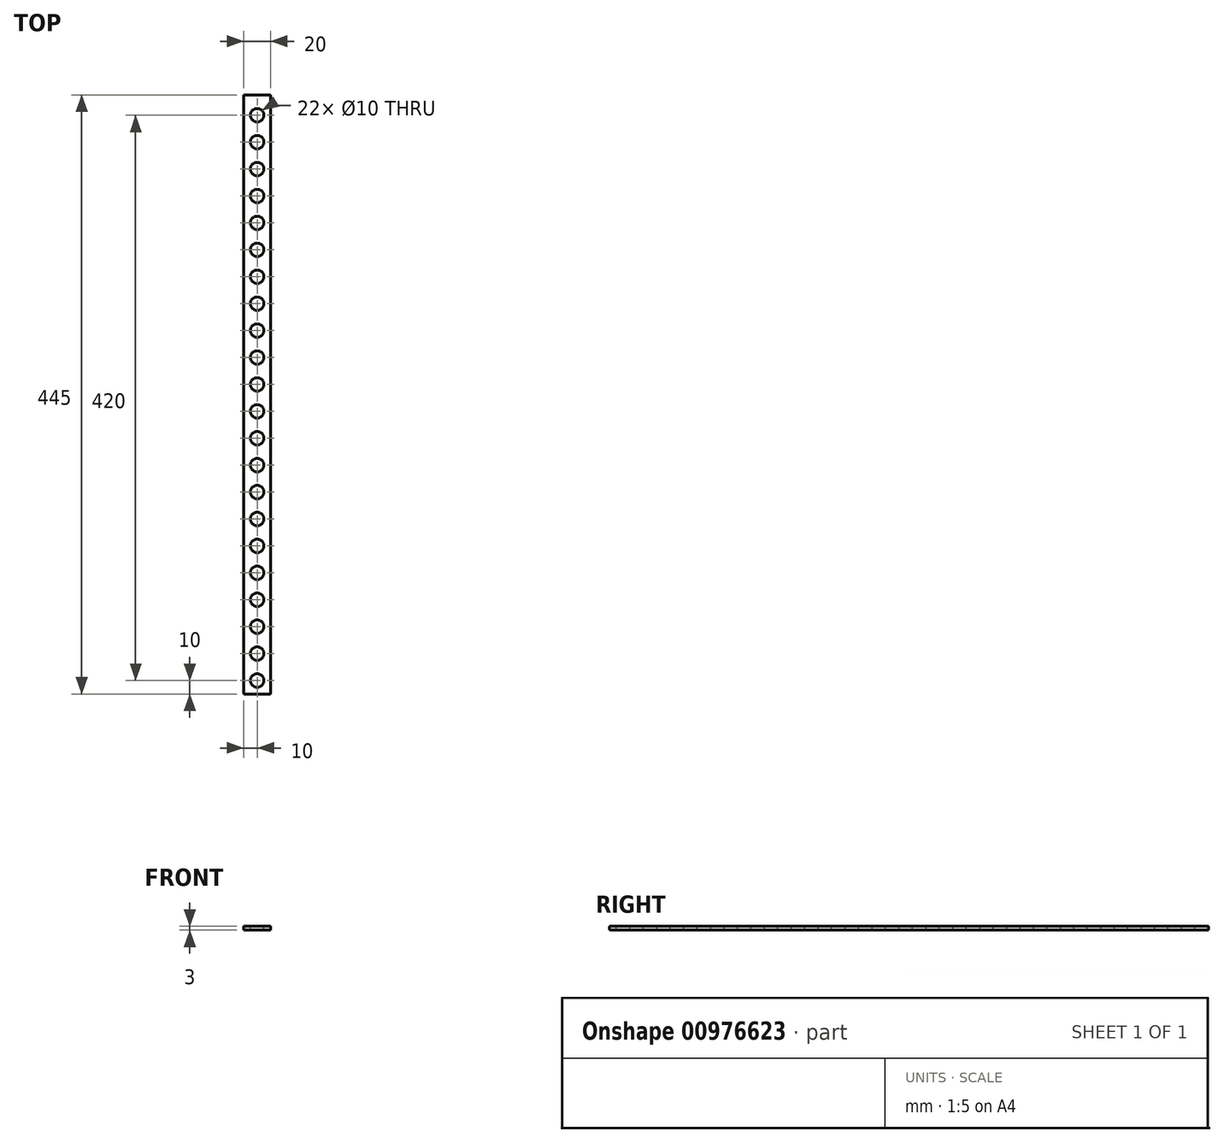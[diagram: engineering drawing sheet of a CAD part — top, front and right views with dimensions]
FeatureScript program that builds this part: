
annotation { "Feature Type Name" : "Feature", "Feature Type Description" : "" }
export const myFeature = defineFeature(function(context is Context, id is Id, definition is map)
    precondition{}
    {
        {
            var Q0;
            Q0=qCreatedBy(makeId("Front.planeOp"),FACE);
            var sketch = newSketch(context, id + "F0", { "sketchPlane" : qUnion([Q0])});
            skLineSegment(sketch, "E0.bottom", {"start": v(10, 1.5) * mm, "end": v(-10, 1.5) * mm});
            skLineSegment(sketch, "E0.top", {"start": v(10, -1.5) * mm, "end": v(-10, -1.5) * mm});
            skLineSegment(sketch, "E0.left", {"start": v(10, 1.5) * mm, "end": v(10, -1.5) * mm});
            skLineSegment(sketch, "E0.right", {"start": v(-10, 1.5) * mm, "end": v(-10, -1.5) * mm});
            skPoint(sketch, "E0.middle", {"position": v(0, 0) * mm});
            skSolve(sketch);
        }
        {
            var Q0;
            Q0=qSketchRegion(id+"F0",true);
            extrude(context, id + "F1", {"entities" : qUnion([Q0]), "depth" : 500 * mm, "offsetDistance" : 25 * mm, "symmetric" : true});
        }
        {
            var Q0;
            Q0=makeQuery(id+"F1.opExtrude","SWEPT_FACE",FACE,{"disambiguationData":[OSD([sQuery(id+"F0.wireOp",EDGE,"E0.bottom")])]});
            var sketch = newSketch(context, id + "F2", { "sketchPlane" : qUnion([Q0])});
            skLineSegment(sketch, "E1", {"start": v(0, -250) * mm, "end": v(0, -240) * mm});
            skCircle(sketch, "E2", {"center": v(0, -235) * mm, "radius": 5 * mm});
            skLineSegment(sketch, "E3", {"start": v(0, -235) * mm, "end": v(0, -215) * mm});
            skCircle(sketch, "E4.1.0.0", {"center": v(0, -215) * mm, "radius": 5 * mm});
            skCircle(sketch, "E4.2.0.0", {"center": v(0, -195) * mm, "radius": 5 * mm});
            skCircle(sketch, "E4.3.0.0", {"center": v(0, -175) * mm, "radius": 5 * mm});
            skCircle(sketch, "E4.4.0.0", {"center": v(0, -155) * mm, "radius": 5 * mm});
            skCircle(sketch, "E4.5.0.0", {"center": v(0, -135) * mm, "radius": 5 * mm});
            skCircle(sketch, "E4.6.0.0", {"center": v(0, -115) * mm, "radius": 5 * mm});
            skCircle(sketch, "E4.7.0.0", {"center": v(0, -95) * mm, "radius": 5 * mm});
            skCircle(sketch, "E4.8.0.0", {"center": v(0, -75) * mm, "radius": 5 * mm});
            skCircle(sketch, "E4.9.0.0", {"center": v(0, -55) * mm, "radius": 5 * mm});
            skCircle(sketch, "E4.10.0.0", {"center": v(0, -35) * mm, "radius": 5 * mm});
            skCircle(sketch, "E4.11.0.0", {"center": v(0, -15) * mm, "radius": 5 * mm});
            skCircle(sketch, "E4.12.0.0", {"center": v(0, 5) * mm, "radius": 5 * mm});
            skCircle(sketch, "E4.13.0.0", {"center": v(0, 25) * mm, "radius": 5 * mm});
            skCircle(sketch, "E4.14.0.0", {"center": v(0, 45) * mm, "radius": 5 * mm});
            skCircle(sketch, "E4.15.0.0", {"center": v(0, 65) * mm, "radius": 5 * mm});
            skCircle(sketch, "E4.16.0.0", {"center": v(0, 85) * mm, "radius": 5 * mm});
            skCircle(sketch, "E4.17.0.0", {"center": v(0, 105) * mm, "radius": 5 * mm});
            skCircle(sketch, "E4.18.0.0", {"center": v(0, 125) * mm, "radius": 5 * mm});
            skCircle(sketch, "E4.19.0.0", {"center": v(0, 145) * mm, "radius": 5 * mm});
            skCircle(sketch, "E4.20.0.0", {"center": v(0, 165) * mm, "radius": 5 * mm});
            skCircle(sketch, "E4.21.0.0", {"center": v(0, 185) * mm, "radius": 5 * mm});
            skCircle(sketch, "E4.22.0.0", {"center": v(0, 205) * mm, "radius": 5 * mm});
            skCircle(sketch, "E4.23.0.0", {"center": v(0, 225) * mm, "radius": 5 * mm});
            skCircle(sketch, "E4.24.0.0", {"center": v(0, 245) * mm, "radius": 5 * mm});
            skLineSegment(sketch, "E4.direction1", {"start": v(0, -235) * mm, "end": v(0, -215) * mm, "construction": true});
            skSolve(sketch);
        }
        {
            var Q0;
            Q0=makeQuery(id+"F1.opExtrude","CAP_FACE",FACE,{"disambiguationData":[OSD([sQuery(id+"F0.wireOp",EDGE,"E0.bottom"),sQuery(id+"F0.wireOp",EDGE,"E0.top"),sQuery(id+"F0.wireOp",EDGE,"E0.left"),sQuery(id+"F0.wireOp",EDGE,"E0.right")])],"isStart":true});
            extrude(context, id + "F3", {"entities" : qUnion([Q0]), "operationType" : NewBodyOperationType.ADD, "depth" : 10 * mm, "offsetDistance" : 25 * mm});
        }
        {
            var Q0;
            {var subQ0=sQuery(id+"F2.wireOp",EDGE,"E2");var subQ1=makeQuery(id+"F2.imprint","IMPRINT",VERTEX,{"disambiguationData":[OD(0.0)],"derivedFrom":subQ0});Q0=makeQuery(id+"F2.imprint","IMPRINT",FACE,{"disambiguationData":[TD([[makeQuery(id+"F2.imprint","IMPRINT",EDGE,{"disambiguationData":[TD([[subQ1,1.0]])],"derivedFrom":subQ0}),1.0]])]});}
            var Q1;
            Q1=makeQuery(id+"F2.imprint","IMPRINT",FACE,{"disambiguationData":[TD([[makeQuery(id+"F2.imprint","IMPRINT",EDGE,{"derivedFrom":sQuery(id+"F2.wireOp",EDGE,"E4.1.0.0")}),1.0]])]});
            var Q2;
            Q2=makeQuery(id+"F2.imprint","IMPRINT",FACE,{"disambiguationData":[TD([[makeQuery(id+"F2.imprint","IMPRINT",EDGE,{"derivedFrom":sQuery(id+"F2.wireOp",EDGE,"E4.2.0.0")}),1.0]])]});
            var Q3;
            Q3=makeQuery(id+"F2.imprint","IMPRINT",FACE,{"disambiguationData":[TD([[makeQuery(id+"F2.imprint","IMPRINT",EDGE,{"derivedFrom":sQuery(id+"F2.wireOp",EDGE,"E4.3.0.0")}),1.0]])]});
            var Q4;
            Q4=makeQuery(id+"F2.imprint","IMPRINT",FACE,{"disambiguationData":[TD([[makeQuery(id+"F2.imprint","IMPRINT",EDGE,{"derivedFrom":sQuery(id+"F2.wireOp",EDGE,"E4.4.0.0")}),1.0]])]});
            var Q5;
            Q5=makeQuery(id+"F2.imprint","IMPRINT",FACE,{"disambiguationData":[TD([[makeQuery(id+"F2.imprint","IMPRINT",EDGE,{"derivedFrom":sQuery(id+"F2.wireOp",EDGE,"E4.5.0.0")}),1.0]])]});
            var Q6;
            Q6=makeQuery(id+"F2.imprint","IMPRINT",FACE,{"disambiguationData":[TD([[makeQuery(id+"F2.imprint","IMPRINT",EDGE,{"derivedFrom":sQuery(id+"F2.wireOp",EDGE,"E4.6.0.0")}),1.0]])]});
            var Q7;
            Q7=makeQuery(id+"F2.imprint","IMPRINT",FACE,{"disambiguationData":[TD([[makeQuery(id+"F2.imprint","IMPRINT",EDGE,{"derivedFrom":sQuery(id+"F2.wireOp",EDGE,"E4.7.0.0")}),1.0]])]});
            var Q8;
            Q8=makeQuery(id+"F2.imprint","IMPRINT",FACE,{"disambiguationData":[TD([[makeQuery(id+"F2.imprint","IMPRINT",EDGE,{"derivedFrom":sQuery(id+"F2.wireOp",EDGE,"E4.8.0.0")}),1.0]])]});
            var Q9;
            Q9=makeQuery(id+"F2.imprint","IMPRINT",FACE,{"disambiguationData":[TD([[makeQuery(id+"F2.imprint","IMPRINT",EDGE,{"derivedFrom":sQuery(id+"F2.wireOp",EDGE,"E4.9.0.0")}),1.0]])]});
            var Q10;
            Q10=makeQuery(id+"F2.imprint","IMPRINT",FACE,{"disambiguationData":[TD([[makeQuery(id+"F2.imprint","IMPRINT",EDGE,{"derivedFrom":sQuery(id+"F2.wireOp",EDGE,"E4.10.0.0")}),1.0]])]});
            var Q11;
            Q11=makeQuery(id+"F2.imprint","IMPRINT",FACE,{"disambiguationData":[TD([[makeQuery(id+"F2.imprint","IMPRINT",EDGE,{"derivedFrom":sQuery(id+"F2.wireOp",EDGE,"E4.11.0.0")}),1.0]])]});
            var Q12;
            Q12=makeQuery(id+"F2.imprint","IMPRINT",FACE,{"disambiguationData":[TD([[makeQuery(id+"F2.imprint","IMPRINT",EDGE,{"derivedFrom":sQuery(id+"F2.wireOp",EDGE,"E4.12.0.0")}),1.0]])]});
            var Q13;
            Q13=makeQuery(id+"F2.imprint","IMPRINT",FACE,{"disambiguationData":[TD([[makeQuery(id+"F2.imprint","IMPRINT",EDGE,{"derivedFrom":sQuery(id+"F2.wireOp",EDGE,"E4.15.0.0")}),1.0]])]});
            var Q14;
            Q14=makeQuery(id+"F2.imprint","IMPRINT",FACE,{"disambiguationData":[TD([[makeQuery(id+"F2.imprint","IMPRINT",EDGE,{"derivedFrom":sQuery(id+"F2.wireOp",EDGE,"E4.16.0.0")}),1.0]])]});
            var Q15;
            Q15=makeQuery(id+"F2.imprint","IMPRINT",FACE,{"disambiguationData":[TD([[makeQuery(id+"F2.imprint","IMPRINT",EDGE,{"derivedFrom":sQuery(id+"F2.wireOp",EDGE,"E4.17.0.0")}),1.0]])]});
            var Q16;
            Q16=makeQuery(id+"F2.imprint","IMPRINT",FACE,{"disambiguationData":[TD([[makeQuery(id+"F2.imprint","IMPRINT",EDGE,{"derivedFrom":sQuery(id+"F2.wireOp",EDGE,"E4.18.0.0")}),1.0]])]});
            var Q17;
            Q17=makeQuery(id+"F2.imprint","IMPRINT",FACE,{"disambiguationData":[TD([[makeQuery(id+"F2.imprint","IMPRINT",EDGE,{"derivedFrom":sQuery(id+"F2.wireOp",EDGE,"E4.14.0.0")}),1.0]])]});
            var Q18;
            Q18=makeQuery(id+"F2.imprint","IMPRINT",FACE,{"disambiguationData":[TD([[makeQuery(id+"F2.imprint","IMPRINT",EDGE,{"derivedFrom":sQuery(id+"F2.wireOp",EDGE,"E4.13.0.0")}),1.0]])]});
            var Q19;
            Q19=makeQuery(id+"F2.imprint","IMPRINT",FACE,{"disambiguationData":[TD([[makeQuery(id+"F2.imprint","IMPRINT",EDGE,{"derivedFrom":sQuery(id+"F2.wireOp",EDGE,"E4.19.0.0")}),1.0]])]});
            var Q20;
            Q20=makeQuery(id+"F2.imprint","IMPRINT",FACE,{"disambiguationData":[TD([[makeQuery(id+"F2.imprint","IMPRINT",EDGE,{"derivedFrom":sQuery(id+"F2.wireOp",EDGE,"E4.20.0.0")}),1.0]])]});
            var Q21;
            Q21=makeQuery(id+"F2.imprint","IMPRINT",FACE,{"disambiguationData":[TD([[makeQuery(id+"F2.imprint","IMPRINT",EDGE,{"derivedFrom":sQuery(id+"F2.wireOp",EDGE,"E4.21.0.0")}),1.0]])]});
            var Q22;
            Q22=makeQuery(id+"F2.imprint","IMPRINT",FACE,{"disambiguationData":[TD([[makeQuery(id+"F2.imprint","IMPRINT",EDGE,{"derivedFrom":sQuery(id+"F2.wireOp",EDGE,"E4.22.0.0")}),1.0]])]});
            var Q23;
            Q23=makeQuery(id+"F2.imprint","IMPRINT",FACE,{"disambiguationData":[TD([[makeQuery(id+"F2.imprint","IMPRINT",EDGE,{"derivedFrom":sQuery(id+"F2.wireOp",EDGE,"E4.23.0.0")}),1.0]])]});
            var Q24;
            Q24=makeQuery(id+"F2.imprint","IMPRINT",FACE,{"disambiguationData":[TD([[makeQuery(id+"F2.imprint","IMPRINT",EDGE,{"derivedFrom":sQuery(id+"F2.wireOp",EDGE,"E4.24.0.0")}),1.0]])]});
            extrude(context, id + "F4", {"entities" : qUnion([Q0, Q1, Q2, Q3, Q4, Q5, Q6, Q7, Q8, Q9, Q10, Q11, Q12, Q13, Q14, Q15, Q16, Q17, Q18, Q19, Q20, Q21, Q22, Q23, Q24]), "operationType" : NewBodyOperationType.REMOVE, "oppositeDirection" : true, "depth" : 3 * mm, "offsetDistance" : 25 * mm});
        }
        {
            var Q0;
            {var subQ0=sQuery(id+"F0.wireOp",EDGE,"E0.left");Q0=makeQuery(id+"F3.boolean.opBoolean","MERGE",FACE,{"derivedFrom":[makeQuery(id+"F1.opExtrude","SWEPT_FACE",FACE,{"disambiguationData":[OSD([subQ0])]}),makeQuery(id+"F3.opExtrude","SWEPT_FACE",FACE,{"disambiguationData":[OSD([subQ0])]})]});}
            var Q1;
            Q1=makeQuery(id+"F1.opExtrude","CAP_FACE",FACE,{"disambiguationData":[OSD([sQuery(id+"F0.wireOp",EDGE,"E0.bottom"),sQuery(id+"F0.wireOp",EDGE,"E0.top"),sQuery(id+"F0.wireOp",EDGE,"E0.left"),sQuery(id+"F0.wireOp",EDGE,"E0.right")])],"isStart":false});
            var Q2;
            {var subQ0=sQuery(id+"F0.wireOp",EDGE,"E0.right");var subQ1=sQuery(id+"F0.wireOp",EDGE,"E0.bottom");Q2=makeQuery(id+"F3.boolean.opBoolean","MERGE",EDGE,{"derivedFrom":[makeQuery(id+"F1.opExtrude","SWEPT_EDGE",EDGE,{"disambiguationData":[OSD([subQ1,subQ0])]}),makeQuery(id+"F3.opExtrude","SWEPT_EDGE",EDGE,{"disambiguationData":[OSD([subQ1,subQ0])]})]});}
            var Q3;
            Q3=makeQuery(id+"F3.opExtrude","CAP_FACE",FACE,{"disambiguationData":[OSD([sQuery(id+"F0.wireOp",EDGE,"E0.bottom"),sQuery(id+"F0.wireOp",EDGE,"E0.top"),sQuery(id+"F0.wireOp",EDGE,"E0.left"),sQuery(id+"F0.wireOp",EDGE,"E0.right")])],"isStart":false});
            fillet(context, id + "F5", {"entities" : qUnion([Q0, Q1, Q2, Q3]), "radius" : .5 * mm, "tangentPropagation" : true, "allowEdgeOverflow" : false});
        }
        {
            var Q0;
            {var subQ0=sQuery(id+"F0.wireOp",EDGE,"E0.top");Q0=makeQuery(id+"F3.boolean.opBoolean","MERGE",FACE,{"derivedFrom":[makeQuery(id+"F1.opExtrude","SWEPT_FACE",FACE,{"disambiguationData":[OSD([subQ0])]}),makeQuery(id+"F3.opExtrude","SWEPT_FACE",FACE,{"disambiguationData":[OSD([subQ0])]})]});}
            var sketch = newSketch(context, id + "F6", { "sketchPlane" : qUnion([Q0])});
            skLineSegment(sketch, "E5", {"start": v(0, 195) * mm, "end": v(0, 185) * mm});
            skLineSegment(sketch, "E6", {"start": v(16.08, 185) * mm, "end": v(-14.65, 185) * mm});
            skLineSegment(sketch, "E7", {"start": v(-14.65, 254.38) * mm, "end": v(32.46, 259.38) * mm});
            skLineSegment(sketch, "E8", {"start": v(32.46, 259.38) * mm, "end": v(16.08, 185) * mm});
            skLineSegment(sketch, "E9", {"start": v(-14.65, 254.38) * mm, "end": v(-14.65, 185) * mm});
            skSolve(sketch);
        }
        {
            var Q0;
            Q0=qSketchRegion(id+"F6",true);
            extrude(context, id + "F7", {"entities" : qUnion([Q0]), "operationType" : NewBodyOperationType.REMOVE, "oppositeDirection" : true, "depth" : 25 * mm, "offsetDistance" : 25 * mm});
        }
        {
            var Q0;
            Q0=makeQuery(id+"F7.boolean.opBoolean","COPY",FACE,{"derivedFrom":makeQuery(id+"F7.opExtrude","SWEPT_FACE",FACE,{"disambiguationData":[OSD([sQuery(id+"F6.wireOp",EDGE,"E6")])]})});
            fillet(context, id + "F8", {"entities" : qUnion([Q0]), "radius" : .5 * mm, "tangentPropagation" : true, "allowEdgeOverflow" : false});
        }
    });
